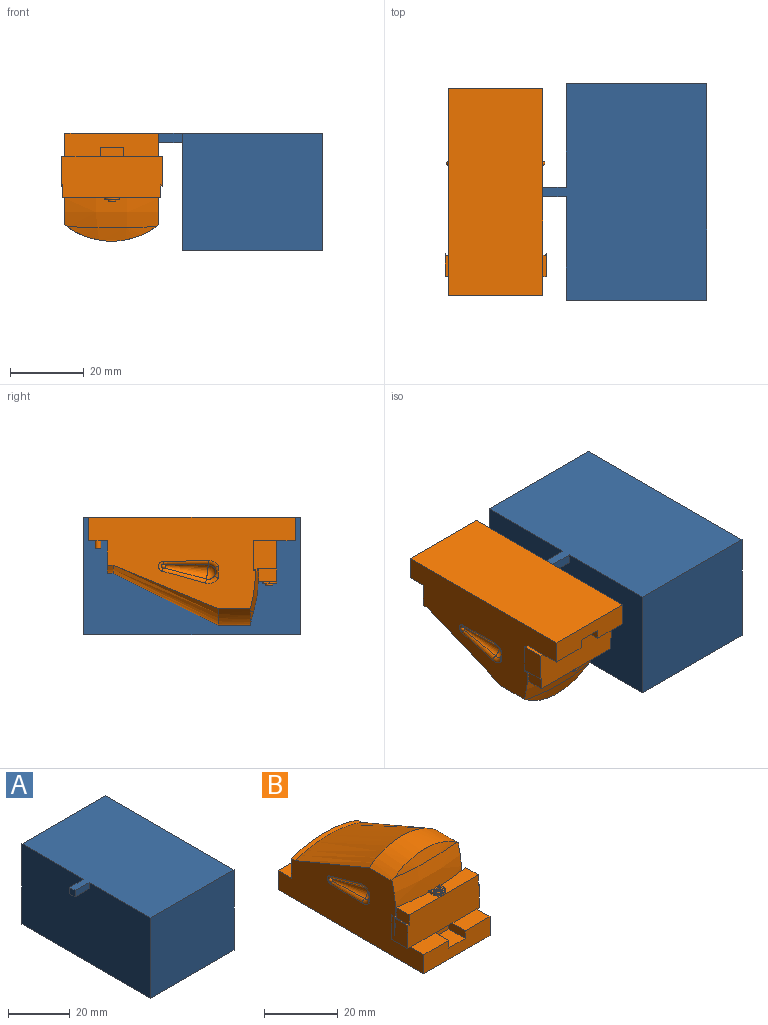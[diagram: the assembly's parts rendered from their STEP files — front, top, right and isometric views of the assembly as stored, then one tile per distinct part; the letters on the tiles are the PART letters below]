
ASSEMBLY  parts=2 mates=1
PART A: 61 faces, bbox 44.5x58.7x31.8 mm
  f0: plane 58.67x31.75mm, normal (-1,0,0), area 1856.4mm2, adj f1,f13,f18,f20,f57,f58,f59
  f1: plane 58.67x38.1mm, normal (0,0,-1), area 973.8mm2, adj f0,f7,f9,f14,f18,f19,f20,f34
  f2: plane 26.68x5.08mm, normal (0,0,-1), area 97.9mm2, adj f3,f4,f6,f34,f41,f42,f43,f44
  f3: plane 5.02x4.45mm, normal (1,0,0), area 21.6mm2, adj f2,f8,f30,f34
  f4: plane 5.02x4.45mm, normal (-1,0,0), area 21.6mm2, adj f2,f32,f33,f34
  f5: bspline ~34.88x14.63mm, area 16.8mm2, adj f7,f21,f24,f50
  f6: revolved ~26.6x7.53mm, area 194.6mm2, adj f2,f26,f27,f28,f30,f32,f42,f44
  f7: plane 45.85x18.66mm, normal (1,0,0), area 606.6mm2, adj f1,f5,f8,f11,f17,f19,f24,f30
  f8: plane 5.29x0.41mm, normal (0,0,-1), area 2mm2, adj f3,f7,f30,f34
  f9: plane 45.85x18.66mm, normal (-1,0,0), area 606.6mm2, adj f1,f10,f15,f19,f22,f23,f32,f33
  f10: cylinder r=0.51mm len=9.14mm, axis (0,1,0), area 4.1mm2, adj f9,f12,f22,f31
  f11: cylinder r=0.51mm len=9.14mm, axis (0,1,0), area 4.1mm2, adj f7,f12,f29,f50
  f12: cylinder r=21.38mm len=27.06mm, axis (0,1,0), area 267.4mm2, adj f10,f11,f21,f25,f26,f28
  f13: plane 58.67x44.45mm, normal (0,0,1), area 2251.6mm2, adj f0,f14,f18,f20,f57,f58,f60
  f14: plane 58.67x31.75mm, normal (1,0,0), area 1862.9mm2, adj f1,f13,f18,f20
  f15: cylinder r=0.51mm len=1.52mm, axis (0,1,0), area 0.9mm2, adj f9,f16,f19,f23
  f16: cylinder r=39.03mm len=26.76mm, axis (0,1,0), area 41.6mm2, adj f15,f17,f19,f21
  f17: cylinder r=0.51mm len=1.52mm, axis (0,1,0), area 0.9mm2, adj f7,f16,f19,f24
  f18: plane 38.1x31.75mm, normal (0,1,0), area 1209.7mm2, adj f0,f1,f13,f14
  f19: plane 27.44x9.81mm, normal (0,-1,0), area 246.4mm2, adj f1,f7,f9,f15,f16,f17
  f20: plane 38.1x31.75mm, normal (0,-1,0), area 1209.7mm2, adj f0,f1,f13,f14
  f21: bspline ~28.45x27.03mm, area 879.2mm2, adj f5,f12,f16,f22
  f22: bspline ~34.88x14.63mm, area 16.9mm2, adj f9,f10,f21,f23
  f23: bspline ~0.48x0.35mm, area 0mm2, adj f9,f15,f22
  f24: bspline ~0.48x0.35mm, area 0mm2, adj f5,f7,f17
  f25: bspline ~29.67x6.22mm, area 18.2mm2, adj f12,f26,f27,f28
  f26: bspline ~2.63x2.18mm, area 0.4mm2, adj f6,f12,f25,f31
  f27: cylinder r=72.14mm len=25.65mm, axis (0,0.27,0.96), area 73mm2, adj f6,f25
  f28: bspline ~2.63x2.18mm, area 0.4mm2, adj f6,f12,f25,f29
  f29: sphere r=0.51mm, area 0.2mm2, adj f11,f28,f30
  f30: torus R=42.91mm, axis (-1,0,0), area 7.9mm2, adj f3,f6,f7,f8,f29
  f31: sphere r=0.51mm, area 0.2mm2, adj f10,f26,f32
  f32: torus R=42.91mm, axis (-1,0,0), area 7.9mm2, adj f4,f6,f9,f31,f33
  f33: plane 5.29x0.41mm, normal (0,0,-1), area 2mm2, adj f4,f9,f32,f34
  f34: plane 27.43x12.07mm, normal (0,1,0), area 327.3mm2, adj f1,f2,f3,f4,f7,f8,f9,f33
  f35: torus R=1.27mm, axis (0,0,1), area 2.8mm2, adj f36,f37
  f36: cylinder r=1.02mm len=2.03mm, axis (0,0,-1), area 2.4mm2, adj f35,f49
  f37: plane 3.56x3.39mm, normal (0,0,-1), area 5.6mm2, adj f35,f38,f39,f40,f47
  f38: cylinder r=0.25mm len=1.61mm, axis (0,-1,0), area 0.6mm2, adj f37,f40,f45,f46
  f39: cylinder r=0.25mm len=1.61mm, axis (0,1,0), area 0.6mm2, adj f37,f40,f43,f48
  f40: torus R=1.78mm, axis (0,0,1), area 2.4mm2, adj f37,f38,f39,f41
  f41: cylinder r=2.03mm len=4.06mm, axis (0,0,-1), area 2.4mm2, adj f2,f40,f43,f45
  f42: torus R=44.87mm, axis (1,0,0), area 0.1mm2, adj f2,f6,f43,f48
  f43: plane 1.56x0.38mm, normal (1,0,0), area 0.6mm2, adj f2,f39,f41,f42
  f44: torus R=44.87mm, axis (1,0,0), area 0.1mm2, adj f2,f6,f45,f46
  f45: plane 1.56x0.38mm, normal (-1,0,0), area 0.6mm2, adj f2,f38,f41,f44
  f46: bspline ~0.62x0.59mm, area 0.2mm2, adj f6,f38,f44,f47
  f47: bspline ~15.23x0.63mm, area 1.3mm2, adj f6,f37,f46,f48
  f48: bspline ~0.62x0.59mm, area 0.2mm2, adj f6,f39,f42,f47
  f49: plane 2.03x2.03mm, normal (0,0,-1), area 2.4mm2, adj f36,f55
  f50: plane 0.45x0.22mm, normal (0,-1,0), area 0mm2, adj f5,f7,f11
  f51: cylinder r=0.79mm len=2.54mm, axis (0,0,-1), area 12.7mm2, adj f1,f52
  f52: plane 1.59x1.59mm, normal (0,0,-1), area 2mm2, adj f51
  f53: cylinder r=0.79mm len=2.54mm, axis (0,0,-1), area 12.7mm2, adj f1,f54
  f54: plane 1.59x1.59mm, normal (0,0,-1), area 2mm2, adj f53
  f55: cylinder r=0.51mm len=1.02mm, axis (0,0,1), area 2.4mm2, adj f49,f56
  f56: plane 1.02x1.02mm, normal (0,0,-1), area 0.8mm2, adj f55
  f57: plane 6.35x2.54mm, normal (0,-1,0), area 16.1mm2, adj f0,f13,f59,f60
  f58: plane 6.35x2.54mm, normal (0,1,0), area 16.1mm2, adj f0,f13,f59,f60
  f59: plane 6.35x2.54mm, normal (0,0,-1), area 16.1mm2, adj f0,f57,f58,f60
  f60: plane 2.54x2.54mm, normal (-1,0,0), area 6.5mm2, adj f13,f57,f58,f59
PART B: 90 faces, bbox 36.6x56.1x29.3 mm
  f0: plane 9.53x5.08mm, normal (0,0,1), area 46.4mm2, adj f9,f15,f65,f70,f86
  f1: plane 9.53x5.08mm, normal (0,0,1), area 48.4mm2, adj f2,f14,f21,f81
  f2: plane 25.4x6.35mm, normal (0,-1,0), area 145.2mm2, adj f1,f9,f14,f66,f67,f81,f82,f83
  f3: revolved ~26.6x3.15mm, area 78.6mm2, adj f4,f5,f16,f17,f23,f42,f74,f75
  f4: bspline ~0.62x0.6mm, area 0.2mm2, adj f3,f17,f28,f74,f77
  f5: bspline ~0.62x0.59mm, area 0.2mm2, adj f3,f17,f30,f75,f78
  f6: plane 6.22x1.02mm, normal (0,0,-1), area 5.9mm2, adj f8,f9,f10,f11,f21
  f7: plane 6.22x1.02mm, normal (0,0,-1), area 5.9mm2, adj f12,f13,f14,f20,f21
  f8: plane 8.13x6.22mm, normal (1,0,0), area 47.9mm2, adj f6,f11,f18,f21,f35,f43
  f9: plane 56.09x24.85mm, normal (1,0,0), area 830.8mm2, adj f0,f2,f6,f10,f15,f37,f38,f39
  f10: plane 7.62x0.51mm, normal (0,1,0), area 3.9mm2, adj f6,f9,f11,f45
  f11: cylinder r=0.51mm len=8.13mm, axis (0,0,-1), area 6.3mm2, adj f6,f8,f10,f43
  f12: cylinder r=0.51mm len=8.13mm, axis (0,0,-1), area 6.3mm2, adj f7,f13,f20,f41
  f13: plane 7.62x0.51mm, normal (0,1,0), area 3.9mm2, adj f7,f12,f14,f45
  f14: plane 56.09x24.85mm, normal (-1,0,0), area 830.8mm2, adj f1,f2,f7,f13,f15,f37,f38,f39
  f15: plane 25.42x8.81mm, normal (0,1,0), area 205mm2, adj f0,f9,f14,f39,f64,f85
  f16: plane 4.93x3.43mm, normal (1,0,0), area 16.6mm2, adj f3,f18,f21,f35,f76
  f17: bspline ~15.23x0.65mm, area 1.5mm2, adj f3,f4,f5,f27
  f18: plane 5.29x0.41mm, normal (0,0,1), area 2mm2, adj f8,f16,f21,f35
  f19: plane 5.29x0.42mm, normal (0,0,1), area 2mm2, adj f20,f21,f23,f24
  f20: plane 8.13x6.22mm, normal (-1,0,0), area 47.9mm2, adj f7,f12,f19,f21,f24,f25,f34,f41
  f21: plane 27.43x11.05mm, normal (0,-1,0), area 300.3mm2, adj f1,f6,f7,f8,f16,f18,f19,f20
  f22: plane 7.19x0.5mm, normal (-0.98,0.18,0), area 2.3mm2, adj f23,f25,f33,f42
  f23: plane 4.93x3.43mm, normal (-1,0,0), area 16.6mm2, adj f3,f19,f21,f22,f76
  f24: cylinder r=0.51mm len=6.02mm, axis (0,0,-1), area 2.1mm2, adj f19,f20,f25
  f25: revolved ~6.7x0.62mm, area 1.9mm2, adj f20,f22,f24,f33,f34
  f26: cylinder r=1.02mm len=2.03mm, axis (0,0,-1), area 2.4mm2, adj f31,f32
  f27: plane 3.56x3.21mm, normal (0,0,1), area 4.9mm2, adj f17,f28,f29,f30,f31
  f28: cylinder r=0.25mm len=1.49mm, axis (0,1,0), area 0.6mm2, adj f4,f27,f29,f77
  f29: torus R=1.78mm, axis (0,0,1), area 2.4mm2, adj f27,f28,f30,f79
  f30: cylinder r=0.25mm len=1.49mm, axis (0,-1,0), area 0.6mm2, adj f5,f27,f29,f78
  f31: torus R=1.27mm, axis (0,0,1), area 2.8mm2, adj f26,f27
  f32: plane 2.03x2.03mm, normal (0,0,1), area 2.4mm2, adj f26,f72
  f33: plane 6.7x0mm, normal (-0.98,0.18,0), area 0mm2, adj f22,f25,f34,f42
  f34: plane 7.21x0.51mm, normal (0,-1,0), area 3.3mm2, adj f20,f25,f33,f41
  f35: cylinder r=0.51mm len=0.51mm, axis (0,0,-1), area 0.4mm2, adj f8,f16,f18,f44
  f36: cylinder r=71.13mm len=24.05mm, axis (0,0.27,0.96), area 0mm2, adj f37,f38
  f37: cylinder r=20.37mm len=25.4mm, axis (0,1,0), area 240mm2, adj f9,f14,f36,f38,f40
  f38: revolved ~25.4x11.58mm, area 296.4mm2, adj f9,f14,f36,f37,f45
  f39: cylinder r=38.01mm len=25.4mm, axis (0,-1,0), area 39.5mm2, adj f9,f14,f15,f40
  f40: bspline ~28.45x25.4mm, area 829.5mm2, adj f9,f14,f37,f39
  f41: cylinder r=0.51mm len=0.93mm, axis (0,1,0), area 0.5mm2, adj f12,f20,f34,f45
  f42: bspline ~36.52x3.65mm, area 21.5mm2, adj f3,f22,f33,f44,f45
  f43: cylinder r=0.51mm len=0.93mm, axis (0,1,0), area 0.5mm2, adj f8,f11,f44,f45
  f44: sphere r=0.51mm, area 0.4mm2, adj f35,f42,f43
  f45: plane 26.44x1.65mm, normal (0,0,1), area 13.4mm2, adj f10,f13,f38,f41,f42,f43
  f46: sphere r=0.56mm, area 4mm2, adj f47,f51
  f47: cone r=0.56mm half-angle=7.2deg, axis (0,-0.99,0.12), area 33.1mm2, adj f46,f48,f50,f52
  f48: sphere r=2.1mm, area 9mm2, adj f47,f49,f53,f54
  f49: torus R=3.12mm, axis (-1,0,0), area 3.7mm2, adj f14,f48,f50,f54
  f50: bspline ~16.67x1.23mm, area 16.1mm2, adj f14,f47,f49,f51
  f51: torus R=1.32mm, axis (-1,0,0), area 2.4mm2, adj f14,f46,f50,f52
  f52: bspline ~16.37x5.29mm, area 16.1mm2, adj f14,f47,f51,f53
  f53: torus R=3.12mm, axis (-1,0,0), area 4.6mm2, adj f14,f48,f52,f54
  f54: bspline ~3.86x1.09mm, area 3.1mm2, adj f14,f48,f49,f53
  f55: sphere r=0.56mm, area 4mm2, adj f56,f60
  f56: cone r=0.56mm half-angle=7.2deg, axis (0,-0.99,0.12), area 33.1mm2, adj f55,f57,f59,f61
  f57: sphere r=2.1mm, area 9mm2, adj f56,f58,f62,f63
  f58: torus R=3.12mm, axis (1,0,0), area 4.6mm2, adj f9,f57,f59,f63
  f59: bspline ~16.37x5.29mm, area 16.1mm2, adj f9,f56,f58,f60
  f60: torus R=1.32mm, axis (1,0,0), area 2.4mm2, adj f9,f55,f59,f61
  f61: bspline ~16.67x1.23mm, area 16.1mm2, adj f9,f56,f60,f62
  f62: torus R=3.12mm, axis (1,0,0), area 3.7mm2, adj f9,f57,f61,f63
  f63: bspline ~3.86x1.09mm, area 3.1mm2, adj f9,f57,f58,f62
  f64: plane 9.53x5.08mm, normal (0,0,1), area 46.4mm2, adj f14,f15,f65,f68,f88
  f65: plane 25.4x6.35mm, normal (0,1,0), area 145.2mm2, adj f0,f9,f14,f64,f66,f86,f87,f88
  f66: plane 56.01x25.4mm, normal (0,0,-1), area 1422.6mm2, adj f2,f9,f14,f65
  f67: plane 9.53x5.08mm, normal (0,0,1), area 48.4mm2, adj f2,f9,f21,f83
  f68: cylinder r=0.79mm len=2.03mm, axis (0,0,-1), area 10.1mm2, adj f64,f69
  f69: plane 1.59x1.59mm, normal (0,0,1), area 2mm2, adj f68
  f70: cylinder r=0.79mm len=2.03mm, axis (0,0,-1), area 10.1mm2, adj f0,f71
  f71: plane 1.59x1.59mm, normal (0,0,1), area 2mm2, adj f70
  f72: cylinder r=0.51mm len=1.02mm, axis (0,0,1), area 3.2mm2, adj f32,f73
  f73: plane 1.02x1.02mm, normal (0,0,1), area 0.8mm2, adj f72
  f74: extruded ~0.59x0.18mm, area 0.1mm2, adj f3,f4,f76,f77
  f75: extruded ~0.59x0.18mm, area 0.1mm2, adj f3,f5,f76,f78
  f76: plane 26.67x4.99mm, normal (0,0,1), area 95.8mm2, adj f3,f16,f21,f23,f74,f75,f77,f78
  f77: plane 1.53x0.64mm, normal (1,0,0), area 1mm2, adj f4,f28,f74,f76,f79
  f78: plane 1.53x0.64mm, normal (-1,0,0), area 1mm2, adj f5,f30,f75,f76,f79
  f79: cylinder r=2.03mm len=4.06mm, axis (0,0,1), area 4.1mm2, adj f29,f76,f77,f78
  f80: plane 6.35x1.27mm, normal (0,0,-1), area 8.1mm2, adj f21,f81,f83,f84
  f81: plane 6.35x2.54mm, normal (1,0,0), area 16.1mm2, adj f1,f2,f80,f82,f84
  f82: plane 6.35x6.35mm, normal (0,0,1), area 40.3mm2, adj f2,f81,f83,f84
  f83: plane 6.35x2.54mm, normal (-1,0,0), area 16.1mm2, adj f2,f67,f80,f82,f84
  f84: plane 6.35x2.54mm, normal (0,-1,0), area 16.1mm2, adj f80,f81,f82,f83
  f85: plane 6.35x1.27mm, normal (0,0,-1), area 8.1mm2, adj f15,f86,f88,f89
  f86: plane 6.35x2.54mm, normal (-1,0,0), area 16.1mm2, adj f0,f65,f85,f87,f89
  f87: plane 6.35x6.35mm, normal (0,0,1), area 40.3mm2, adj f65,f86,f88,f89
  f88: plane 6.35x2.54mm, normal (1,0,0), area 16.1mm2, adj f64,f65,f85,f87,f89
  f89: plane 6.35x2.54mm, normal (0,1,0), area 16.1mm2, adj f85,f86,f87,f88
PLACE A at identity
PLACE B rot(axis=(0,1,0),180deg) t=(-38.1,-0.06,25.4)mm
MATE planar B.f14 <-> A.f60  axis (1,0,0) through (-25.4,6.99,31.75)mm
